# Revit family: DC_Rheem_PLM_Raypak_B0200ID
name_source: partatom
category: Plumbing Fixtures
units: mm (PartAtom-declared; Revit-internal decimal feet)

## family parameters
Cut with Voids When Loaded = No
Host = Face
Part Type = Normal
Room Calculation Point = No
Round Connector Dimension = Use Radius
Shared = No

## types (4) — shared parameters
Basae2Distance_ANZRS = 105 mm
Base1Distance_ANZRS = 30 mm
BaseWidth_ANZRS = 50 mm  [stored 0.164042 ft]
BoxHeight_ANZRS = 985 mm
ColdWaterConnectionDistance_ANZRS = 215 mm
ColdWaterInletDiameter_ANZRS = 40 mm
ColdWaterInletRadius_ANZRS = 20 mm
ConnectionHeight_ANZRS = 700 mm
GasConnectionDistance_ANZRS = 105 mm
GasInletHeight_ANZRS = 370 mm
H1_ANZRS = 940 mm
Height_ANZRS = 1625 mm  [stored 5.33136 ft]
HotWaterConnectionDistance_ANZRS = 170 mm
HotWaterOutlet Radius_ANZRS = 20 mm
HotWaterOutletDiameter_ANZRS = 40 mm
Length_ANZRS = 675 mm  [stored 2.21457 ft]
Manufacturer = Raypak
Materials_ANZRS = Raypak - Grey Powder Coated Steel
PRVDistance_ANZRS = 210 mm  [stored 0.688976 ft]
PRV_ANZRS = 15 mm  [stored 0.0492126 ft]
URL = http://www.rheem.com.au
Width_ANZRS = 465 mm  [stored 1.52559 ft]
zero-valued in all types: Default Elevation

## per-type parameters (varying)
| type | GasInletDiameter_ANZRS | GasInletRadius_ANZRS | Model | Type Comments |
| Raypak - Gas Water Heater- Indoor - 196 MJ/h  Natural gas, modulating gas control | 25 mm  [stored 0.082021 ft] | 13 mm | B0200NCM/ID | Recovery 750L/h @ 50°C rise |
| Raypak - Gas Water Heater- Indoor - 196 MJ/h  Natural gas, On/Off gas control | 20 mm | 10 mm  [stored 0.0328084 ft] | B0200NCO/ID | Recovery 750L/h @ 50°C rise |
| Raypak - Gas Water Heater- Indoor - 185 MJ/h  Propane gas, modulating gas control | 20 mm | 10 mm  [stored 0.0328084 ft] | B0200PCM/ID | Recovery 705L/h @ 50°C rise |
| Raypak - Gas Water Heater- Indoor - 185 MJ/h  Propane gas, On/Off gas control | 20 mm | 10 mm  [stored 0.0328084 ft] | B0200PCO/ID | Recovery 705L/h @ 50°C rise |

note: column(s) folded — value = type name in every type: Description

note: [stored X ft] marks values corroborated as IEEE doubles in the binary element streams (Revit-internal decimal feet)

## geometry (parser evidence)
native form markers: Blend x6, Sweep x2
no freeform markers — native parametric forms only
